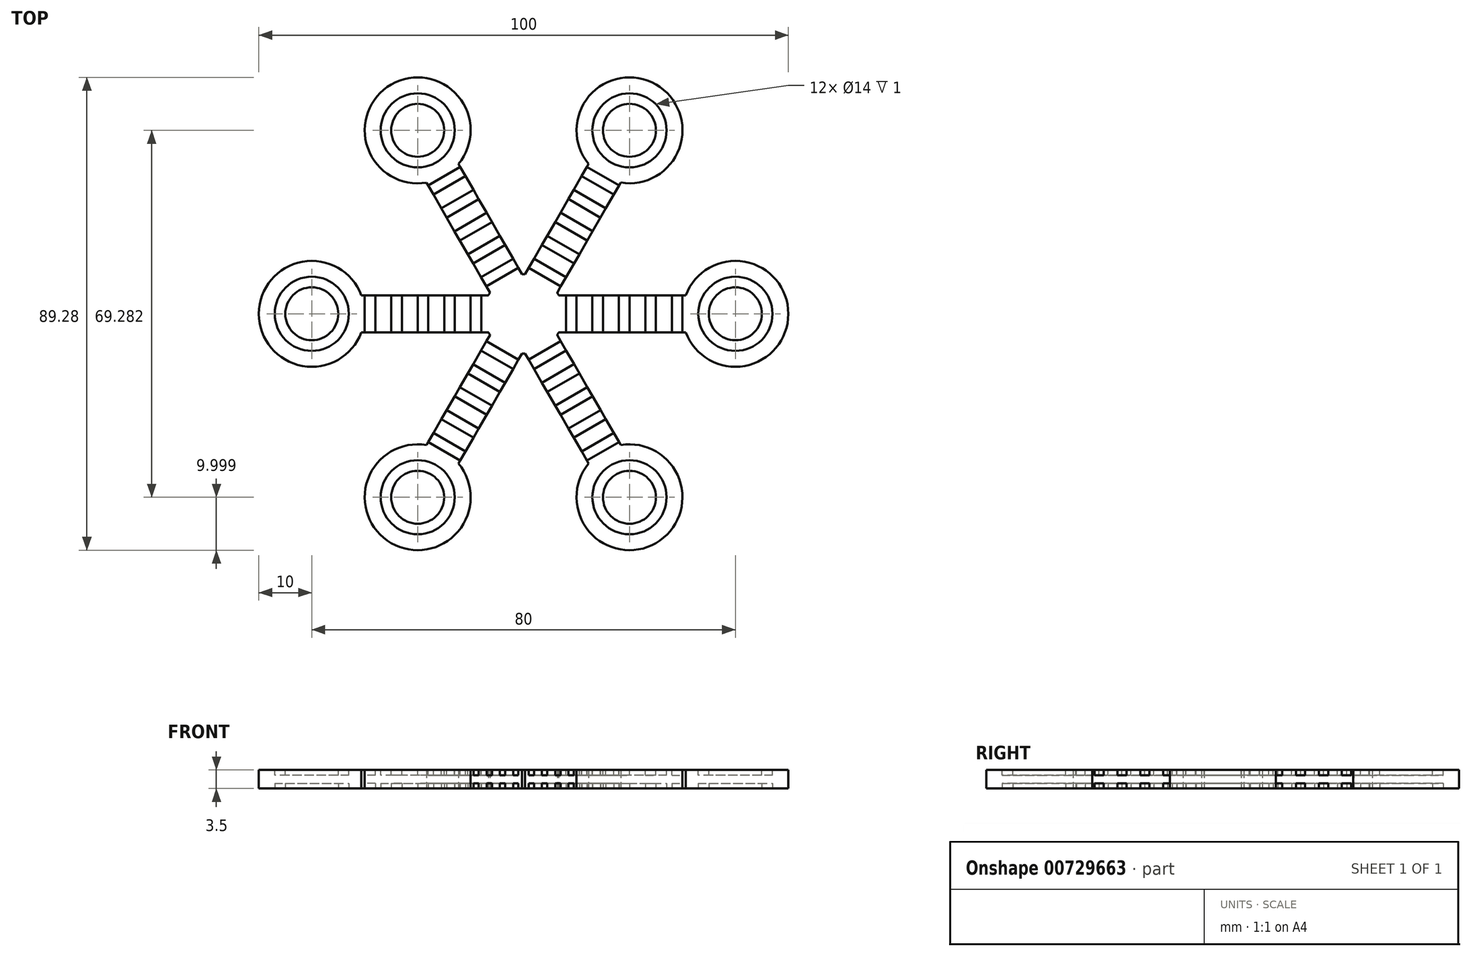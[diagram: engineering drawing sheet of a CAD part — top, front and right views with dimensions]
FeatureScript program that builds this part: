
annotation { "Feature Type Name" : "Feature", "Feature Type Description" : "" }
export const myFeature = defineFeature(function(context is Context, id is Id, definition is map)
    precondition{}
    {
        {
            var Q0;
            Q0=qCreatedBy(makeId("Top.planeOp"),FACE);
            var sketch = newSketch(context, id + "F0", { "sketchPlane" : qUnion([Q0])});
            skCircle(sketch, "E0", {"center": v(0, 0) * mm, "radius": 7.5 * mm});
            skLineSegment(sketch, "E1.bottom", {"start": v(6.63, 3.5) * mm, "end": v(40.15, 3.5) * mm});
            skLineSegment(sketch, "E1.top", {"start": v(6.64, -3.5) * mm, "end": v(39.85, -3.5) * mm});
            skLineSegment(sketch, "E1.right", {"start": v(40.15, 3.5) * mm, "end": v(39.85, -3.5) * mm});
            skCircle(sketch, "E2", {"center": v(40, 0) * mm, "radius": 10 * mm});
            skLineSegment(sketch, "E3.1.0", {"start": v(0.29, 7.5) * mm, "end": v(17.05, 36.52) * mm});
            skLineSegment(sketch, "E3.1.1", {"start": v(6.34, 4) * mm, "end": v(22.95, 32.76) * mm});
            skCircle(sketch, "E3.1.2", {"center": v(20, 34.64) * mm, "radius": 10 * mm});
            skLineSegment(sketch, "E3.1.3", {"start": v(17.05, 36.52) * mm, "end": v(22.95, 32.76) * mm});
            skLineSegment(sketch, "E3.2.0", {"start": v(-6.35, 4) * mm, "end": v(-23.1, 33.02) * mm});
            skLineSegment(sketch, "E3.2.1", {"start": v(-0.3, 7.5) * mm, "end": v(-16.9, 36.26) * mm});
            skCircle(sketch, "E3.2.2", {"center": v(-20, 34.64) * mm, "radius": 10 * mm});
            skLineSegment(sketch, "E3.2.3", {"start": v(-23.1, 33.02) * mm, "end": v(-16.9, 36.26) * mm});
            skLineSegment(sketch, "E3.3.0", {"start": v(-6.63, -3.5) * mm, "end": v(-40.15, -3.5) * mm});
            skLineSegment(sketch, "E3.3.1", {"start": v(-6.64, 3.5) * mm, "end": v(-39.85, 3.5) * mm});
            skCircle(sketch, "E3.3.2", {"center": v(-40, 0) * mm, "radius": 10 * mm});
            skLineSegment(sketch, "E3.3.3", {"start": v(-40.15, -3.5) * mm, "end": v(-39.85, 3.5) * mm});
            skLineSegment(sketch, "E3.4.0", {"start": v(-0.29, -7.5) * mm, "end": v(-17.05, -36.52) * mm});
            skLineSegment(sketch, "E3.4.1", {"start": v(-6.34, -4) * mm, "end": v(-22.95, -32.76) * mm});
            skCircle(sketch, "E3.4.2", {"center": v(-20, -34.64) * mm, "radius": 10 * mm});
            skLineSegment(sketch, "E3.4.3", {"start": v(-17.05, -36.52) * mm, "end": v(-22.95, -32.76) * mm});
            skLineSegment(sketch, "E3.5.0", {"start": v(6.35, -4) * mm, "end": v(23.1, -33.02) * mm});
            skLineSegment(sketch, "E3.5.1", {"start": v(0.3, -7.5) * mm, "end": v(16.9, -36.26) * mm});
            skCircle(sketch, "E3.5.2", {"center": v(20, -34.64) * mm, "radius": 10 * mm});
            skLineSegment(sketch, "E3.5.3", {"start": v(23.1, -33.02) * mm, "end": v(16.9, -36.26) * mm});
            skSolve(sketch);
        }
        {
            var Q0;
            {var subQ0=sQuery(id+"F0.wireOp",EDGE,"E3.3.3");Q0=makeQuery(id+"F0.imprint","IMPRINT",FACE,{"disambiguationData":[TD([[makeQuery(id+"F0.imprint","IMPRINT",EDGE,{"derivedFrom":subQ0}),1.0]])]});}
            var Q1;
            {var subQ0=sQuery(id+"F0.wireOp",EDGE,"E3.3.0");var subQ1=sQuery(id+"F0.wireOp",EDGE,"E0");var subQ2=makeQuery(id+"F0.imprint","INTERSECT",VERTEX,{"derivedFrom":[subQ1,subQ0]});Q1=makeQuery(id+"F0.imprint","IMPRINT",FACE,{"disambiguationData":[TD([[makeQuery(id+"F0.imprint","IMPRINT",EDGE,{"disambiguationData":[TD([[subQ2,1.0]])],"derivedFrom":subQ1}),-1.0]])]});}
            var Q2;
            {var subQ0=sQuery(id+"F0.wireOp",EDGE,"E3.2.3");Q2=makeQuery(id+"F0.imprint","IMPRINT",FACE,{"disambiguationData":[TD([[makeQuery(id+"F0.imprint","IMPRINT",EDGE,{"derivedFrom":subQ0}),1.0]])]});}
            var Q3;
            {var subQ0=sQuery(id+"F0.wireOp",EDGE,"E3.2.3");Q3=makeQuery(id+"F0.imprint","IMPRINT",FACE,{"disambiguationData":[TD([[makeQuery(id+"F0.imprint","IMPRINT",EDGE,{"derivedFrom":subQ0}),-1.0]])]});}
            var Q4;
            {var subQ0=sQuery(id+"F0.wireOp",EDGE,"E3.3.3");Q4=makeQuery(id+"F0.imprint","IMPRINT",FACE,{"disambiguationData":[TD([[makeQuery(id+"F0.imprint","IMPRINT",EDGE,{"derivedFrom":subQ0}),-1.0]])]});}
            var Q5;
            {var subQ0=sQuery(id+"F0.wireOp",EDGE,"E3.1.3");Q5=makeQuery(id+"F0.imprint","IMPRINT",FACE,{"disambiguationData":[TD([[makeQuery(id+"F0.imprint","IMPRINT",EDGE,{"derivedFrom":subQ0}),1.0]])]});}
            var Q6;
            {var subQ0=sQuery(id+"F0.wireOp",EDGE,"E3.1.3");Q6=makeQuery(id+"F0.imprint","IMPRINT",FACE,{"disambiguationData":[TD([[makeQuery(id+"F0.imprint","IMPRINT",EDGE,{"derivedFrom":subQ0}),-1.0]])]});}
            var Q7;
            {var subQ0=sQuery(id+"F0.wireOp",EDGE,"E3.1.0");var subQ1=sQuery(id+"F0.wireOp",EDGE,"E0");var subQ2=makeQuery(id+"F0.imprint","INTERSECT",VERTEX,{"derivedFrom":[subQ1,subQ0]});Q7=makeQuery(id+"F0.imprint","IMPRINT",FACE,{"disambiguationData":[TD([[makeQuery(id+"F0.imprint","IMPRINT",EDGE,{"disambiguationData":[TD([[subQ2,1.0]])],"derivedFrom":subQ1}),-1.0]])]});}
            var Q8;
            {var subQ0=sQuery(id+"F0.wireOp",EDGE,"E0");var subQ8=makeQuery(id+"F0.imprint","INTERSECT",VERTEX,{"derivedFrom":[subQ0,sQuery(id+"F0.wireOp",EDGE,"E1.bottom")]});Q8=makeQuery(id+"F0.imprint","IMPRINT",FACE,{"disambiguationData":[TD([[makeQuery(id+"F0.imprint","IMPRINT",EDGE,{"disambiguationData":[TD([[subQ8,-1.0]])],"derivedFrom":subQ0}),1.0]])]});}
            var Q9;
            {var subQ0=sQuery(id+"F0.wireOp",EDGE,"E1.bottom");var subQ1=sQuery(id+"F0.wireOp",EDGE,"E0");var subQ2=makeQuery(id+"F0.imprint","INTERSECT",VERTEX,{"derivedFrom":[subQ1,subQ0]});Q9=makeQuery(id+"F0.imprint","IMPRINT",FACE,{"disambiguationData":[TD([[makeQuery(id+"F0.imprint","IMPRINT",EDGE,{"disambiguationData":[TD([[subQ2,1.0]])],"derivedFrom":subQ1}),-1.0]])]});}
            var Q10;
            {var subQ0=sQuery(id+"F0.wireOp",EDGE,"E1.right");Q10=makeQuery(id+"F0.imprint","IMPRINT",FACE,{"disambiguationData":[TD([[makeQuery(id+"F0.imprint","IMPRINT",EDGE,{"derivedFrom":subQ0}),-1.0]])]});}
            var Q11;
            {var subQ0=sQuery(id+"F0.wireOp",EDGE,"E1.right");Q11=makeQuery(id+"F0.imprint","IMPRINT",FACE,{"disambiguationData":[TD([[makeQuery(id+"F0.imprint","IMPRINT",EDGE,{"derivedFrom":subQ0}),1.0]])]});}
            var Q12;
            {var subQ0=sQuery(id+"F0.wireOp",EDGE,"E3.5.3");Q12=makeQuery(id+"F0.imprint","IMPRINT",FACE,{"disambiguationData":[TD([[makeQuery(id+"F0.imprint","IMPRINT",EDGE,{"derivedFrom":subQ0}),1.0]])]});}
            var Q13;
            {var subQ0=sQuery(id+"F0.wireOp",EDGE,"E3.5.3");Q13=makeQuery(id+"F0.imprint","IMPRINT",FACE,{"disambiguationData":[TD([[makeQuery(id+"F0.imprint","IMPRINT",EDGE,{"derivedFrom":subQ0}),-1.0]])]});}
            var Q14;
            {var subQ0=sQuery(id+"F0.wireOp",EDGE,"E3.5.0");var subQ1=sQuery(id+"F0.wireOp",EDGE,"E0");var subQ2=makeQuery(id+"F0.imprint","INTERSECT",VERTEX,{"derivedFrom":[subQ1,subQ0]});Q14=makeQuery(id+"F0.imprint","IMPRINT",FACE,{"disambiguationData":[TD([[makeQuery(id+"F0.imprint","IMPRINT",EDGE,{"disambiguationData":[TD([[subQ2,1.0]])],"derivedFrom":subQ1}),-1.0]])]});}
            var Q15;
            {var subQ0=sQuery(id+"F0.wireOp",EDGE,"E3.4.0");var subQ1=sQuery(id+"F0.wireOp",EDGE,"E0");var subQ2=makeQuery(id+"F0.imprint","INTERSECT",VERTEX,{"derivedFrom":[subQ1,subQ0]});Q15=makeQuery(id+"F0.imprint","IMPRINT",FACE,{"disambiguationData":[TD([[makeQuery(id+"F0.imprint","IMPRINT",EDGE,{"disambiguationData":[TD([[subQ2,1.0]])],"derivedFrom":subQ1}),-1.0]])]});}
            var Q16;
            {var subQ0=sQuery(id+"F0.wireOp",EDGE,"E3.4.3");Q16=makeQuery(id+"F0.imprint","IMPRINT",FACE,{"disambiguationData":[TD([[makeQuery(id+"F0.imprint","IMPRINT",EDGE,{"derivedFrom":subQ0}),-1.0]])]});}
            var Q17;
            {var subQ0=sQuery(id+"F0.wireOp",EDGE,"E3.4.3");Q17=makeQuery(id+"F0.imprint","IMPRINT",FACE,{"disambiguationData":[TD([[makeQuery(id+"F0.imprint","IMPRINT",EDGE,{"derivedFrom":subQ0}),1.0]])]});}
            var Q18;
            {var subQ0=sQuery(id+"F0.wireOp",EDGE,"E3.2.0");var subQ1=sQuery(id+"F0.wireOp",EDGE,"E0");var subQ2=makeQuery(id+"F0.imprint","INTERSECT",VERTEX,{"derivedFrom":[subQ1,subQ0]});Q18=makeQuery(id+"F0.imprint","IMPRINT",FACE,{"disambiguationData":[TD([[makeQuery(id+"F0.imprint","IMPRINT",EDGE,{"disambiguationData":[TD([[subQ2,1.0]])],"derivedFrom":subQ1}),-1.0]])]});}
            extrude(context, id + "F1", {"entities" : qUnion([Q0, Q1, Q2, Q3, Q4, Q5, Q6, Q7, Q8, Q9, Q10, Q11, Q12, Q13, Q14, Q15, Q16, Q17, Q18]), "depth" : 3.5 * mm, "offsetDistance" : 25 * mm});
        }
        {
            var Q0;
            Q0=makeQuery(id+"F1.opExtrude","CAP_FACE",FACE,{"disambiguationData":[OSD([sQuery(id+"F0.wireOp",EDGE,"E0"),sQuery(id+"F0.wireOp",EDGE,"E1.bottom"),sQuery(id+"F0.wireOp",EDGE,"E1.top"),sQuery(id+"F0.wireOp",EDGE,"E2"),sQuery(id+"F0.wireOp",EDGE,"E3.1.0"),sQuery(id+"F0.wireOp",EDGE,"E3.1.1"),sQuery(id+"F0.wireOp",EDGE,"E3.1.2"),sQuery(id+"F0.wireOp",EDGE,"E3.2.0"),sQuery(id+"F0.wireOp",EDGE,"E3.2.1"),sQuery(id+"F0.wireOp",EDGE,"E3.2.2"),sQuery(id+"F0.wireOp",EDGE,"E3.3.0"),sQuery(id+"F0.wireOp",EDGE,"E3.3.1"),sQuery(id+"F0.wireOp",EDGE,"E3.3.2"),sQuery(id+"F0.wireOp",EDGE,"E3.4.0"),sQuery(id+"F0.wireOp",EDGE,"E3.4.1"),sQuery(id+"F0.wireOp",EDGE,"E3.4.2"),sQuery(id+"F0.wireOp",EDGE,"E3.5.0"),sQuery(id+"F0.wireOp",EDGE,"E3.5.1"),sQuery(id+"F0.wireOp",EDGE,"E3.5.2")])],"isStart":false});
            var sketch = newSketch(context, id + "F2", { "sketchPlane" : qUnion([Q0])});
            skLineSegment(sketch, "E4.bottom", {"start": v(8, 3.5) * mm, "end": v(10, 3.5) * mm});
            skLineSegment(sketch, "E4.top", {"start": v(8, -3.5) * mm, "end": v(10, -3.5) * mm});
            skLineSegment(sketch, "E4.left", {"start": v(8, 3.5) * mm, "end": v(8, -3.5) * mm});
            skLineSegment(sketch, "E4.right", {"start": v(10, 3.5) * mm, "end": v(10, -3.5) * mm});
            skLineSegment(sketch, "E5.1.0.0", {"start": v(13, -3.5) * mm, "end": v(15, -3.5) * mm});
            skLineSegment(sketch, "E5.1.0.1", {"start": v(13, 3.5) * mm, "end": v(15, 3.5) * mm});
            skLineSegment(sketch, "E5.1.0.2", {"start": v(13, 3.5) * mm, "end": v(13, -3.5) * mm});
            skLineSegment(sketch, "E5.1.0.3", {"start": v(15, 3.5) * mm, "end": v(15, -3.5) * mm});
            skLineSegment(sketch, "E5.2.0.0", {"start": v(18, -3.5) * mm, "end": v(20, -3.5) * mm});
            skLineSegment(sketch, "E5.2.0.1", {"start": v(18, 3.5) * mm, "end": v(20, 3.5) * mm});
            skLineSegment(sketch, "E5.2.0.2", {"start": v(18, 3.5) * mm, "end": v(18, -3.5) * mm});
            skLineSegment(sketch, "E5.2.0.3", {"start": v(20, 3.5) * mm, "end": v(20, -3.5) * mm});
            skLineSegment(sketch, "E5.3.0.0", {"start": v(23, -3.5) * mm, "end": v(25, -3.5) * mm});
            skLineSegment(sketch, "E5.3.0.1", {"start": v(23, 3.5) * mm, "end": v(25, 3.5) * mm});
            skLineSegment(sketch, "E5.3.0.2", {"start": v(23, 3.5) * mm, "end": v(23, -3.5) * mm});
            skLineSegment(sketch, "E5.3.0.3", {"start": v(25, 3.5) * mm, "end": v(25, -3.5) * mm});
            skLineSegment(sketch, "E5.4.0.0", {"start": v(28, -3.5) * mm, "end": v(30, -3.5) * mm});
            skLineSegment(sketch, "E5.4.0.1", {"start": v(28, 3.5) * mm, "end": v(30, 3.5) * mm});
            skLineSegment(sketch, "E5.4.0.2", {"start": v(28, 3.5) * mm, "end": v(28, -3.5) * mm});
            skLineSegment(sketch, "E5.4.0.3", {"start": v(30, 3.5) * mm, "end": v(30, -3.5) * mm});
            skLineSegment(sketch, "E5.direction1", {"start": v(8, -3.5) * mm, "end": v(13, -3.5) * mm, "construction": true});
            skLineSegment(sketch, "E6.1.0", {"start": v(3.47, 13) * mm, "end": v(9.53, 9.51) * mm});
            skLineSegment(sketch, "E6.1.1", {"start": v(0.97, 8.68) * mm, "end": v(1.97, 10.41) * mm});
            skLineSegment(sketch, "E6.1.2", {"start": v(4.47, 14.74) * mm, "end": v(10.53, 11.24) * mm});
            skLineSegment(sketch, "E6.1.3", {"start": v(12.03, 13.84) * mm, "end": v(13.03, 15.57) * mm});
            skLineSegment(sketch, "E6.1.4", {"start": v(0.97, 8.68) * mm, "end": v(7.03, 5.18) * mm});
            skLineSegment(sketch, "E6.1.5", {"start": v(5.97, 17.34) * mm, "end": v(6.97, 19.07) * mm});
            skLineSegment(sketch, "E6.1.6", {"start": v(7.03, 5.18) * mm, "end": v(9.53, 9.51) * mm, "construction": true});
            skLineSegment(sketch, "E6.1.7", {"start": v(1.97, 10.41) * mm, "end": v(8.03, 6.91) * mm});
            skLineSegment(sketch, "E6.1.8", {"start": v(9.47, 23.4) * mm, "end": v(15.53, 19.9) * mm});
            skLineSegment(sketch, "E6.1.9", {"start": v(5.97, 17.34) * mm, "end": v(12.03, 13.84) * mm});
            skLineSegment(sketch, "E6.1.10", {"start": v(11.97, 27.73) * mm, "end": v(18.03, 24.23) * mm});
            skLineSegment(sketch, "E6.1.11", {"start": v(9.53, 9.51) * mm, "end": v(10.53, 11.24) * mm});
            skLineSegment(sketch, "E6.1.12", {"start": v(8.47, 21.67) * mm, "end": v(9.47, 23.4) * mm});
            skLineSegment(sketch, "E6.1.13", {"start": v(6.97, 19.07) * mm, "end": v(13.03, 15.57) * mm});
            skLineSegment(sketch, "E6.1.14", {"start": v(10.97, 26) * mm, "end": v(17.03, 22.5) * mm});
            skLineSegment(sketch, "E6.1.15", {"start": v(3.47, 13) * mm, "end": v(4.47, 14.74) * mm});
            skLineSegment(sketch, "E6.1.16", {"start": v(8.47, 21.67) * mm, "end": v(14.53, 18.17) * mm});
            skLineSegment(sketch, "E6.1.17", {"start": v(14.53, 18.17) * mm, "end": v(15.53, 19.9) * mm});
            skLineSegment(sketch, "E6.1.18", {"start": v(10.97, 26) * mm, "end": v(11.97, 27.73) * mm});
            skLineSegment(sketch, "E6.1.19", {"start": v(17.03, 22.5) * mm, "end": v(18.03, 24.23) * mm});
            skLineSegment(sketch, "E6.1.20", {"start": v(7.03, 5.18) * mm, "end": v(8.03, 6.91) * mm});
            skLineSegment(sketch, "E6.2.0", {"start": v(-9.53, 9.5) * mm, "end": v(-3.47, 13) * mm});
            skLineSegment(sketch, "E6.2.1", {"start": v(-7.03, 5.18) * mm, "end": v(-8.03, 6.91) * mm});
            skLineSegment(sketch, "E6.2.2", {"start": v(-10.53, 11.24) * mm, "end": v(-4.47, 14.74) * mm});
            skLineSegment(sketch, "E6.2.3", {"start": v(-5.97, 17.34) * mm, "end": v(-6.97, 19.07) * mm});
            skLineSegment(sketch, "E6.2.4", {"start": v(-7.03, 5.18) * mm, "end": v(-0.97, 8.67) * mm});
            skLineSegment(sketch, "E6.2.5", {"start": v(-12.03, 13.84) * mm, "end": v(-13.03, 15.57) * mm});
            skLineSegment(sketch, "E6.2.6", {"start": v(-0.97, 8.67) * mm, "end": v(-3.47, 13) * mm, "construction": true});
            skLineSegment(sketch, "E6.2.7", {"start": v(-8.03, 6.91) * mm, "end": v(-1.97, 10.4) * mm});
            skLineSegment(sketch, "E6.2.8", {"start": v(-15.53, 19.9) * mm, "end": v(-9.47, 23.4) * mm});
            skLineSegment(sketch, "E6.2.9", {"start": v(-12.03, 13.84) * mm, "end": v(-5.97, 17.34) * mm});
            skLineSegment(sketch, "E6.2.10", {"start": v(-18.03, 24.23) * mm, "end": v(-11.97, 27.73) * mm});
            skLineSegment(sketch, "E6.2.11", {"start": v(-3.47, 13) * mm, "end": v(-4.47, 14.74) * mm});
            skLineSegment(sketch, "E6.2.12", {"start": v(-14.53, 18.17) * mm, "end": v(-15.53, 19.9) * mm});
            skLineSegment(sketch, "E6.2.13", {"start": v(-13.03, 15.57) * mm, "end": v(-6.97, 19.07) * mm});
            skLineSegment(sketch, "E6.2.14", {"start": v(-17.03, 22.5) * mm, "end": v(-10.97, 26) * mm});
            skLineSegment(sketch, "E6.2.15", {"start": v(-9.53, 9.5) * mm, "end": v(-10.53, 11.24) * mm});
            skLineSegment(sketch, "E6.2.16", {"start": v(-14.53, 18.17) * mm, "end": v(-8.47, 21.67) * mm});
            skLineSegment(sketch, "E6.2.17", {"start": v(-8.47, 21.67) * mm, "end": v(-9.47, 23.4) * mm});
            skLineSegment(sketch, "E6.2.18", {"start": v(-17.03, 22.5) * mm, "end": v(-18.03, 24.23) * mm});
            skLineSegment(sketch, "E6.2.19", {"start": v(-10.97, 26) * mm, "end": v(-11.97, 27.73) * mm});
            skLineSegment(sketch, "E6.2.20", {"start": v(-0.97, 8.67) * mm, "end": v(-1.97, 10.4) * mm});
            skLineSegment(sketch, "E6.3.0", {"start": v(-13, -3.5) * mm, "end": v(-13, 3.5) * mm});
            skLineSegment(sketch, "E6.3.1", {"start": v(-8, -3.5) * mm, "end": v(-10, -3.5) * mm});
            skLineSegment(sketch, "E6.3.2", {"start": v(-15, -3.5) * mm, "end": v(-15, 3.5) * mm});
            skLineSegment(sketch, "E6.3.3", {"start": v(-18, 3.5) * mm, "end": v(-20, 3.5) * mm});
            skLineSegment(sketch, "E6.3.4", {"start": v(-8, -3.5) * mm, "end": v(-8, 3.5) * mm});
            skLineSegment(sketch, "E6.3.5", {"start": v(-18, -3.5) * mm, "end": v(-20, -3.5) * mm});
            skLineSegment(sketch, "E6.3.6", {"start": v(-8, 3.5) * mm, "end": v(-13, 3.5) * mm, "construction": true});
            skLineSegment(sketch, "E6.3.7", {"start": v(-10, -3.5) * mm, "end": v(-10, 3.5) * mm});
            skLineSegment(sketch, "E6.3.8", {"start": v(-25, -3.5) * mm, "end": v(-25, 3.5) * mm});
            skLineSegment(sketch, "E6.3.9", {"start": v(-18, -3.5) * mm, "end": v(-18, 3.5) * mm});
            skLineSegment(sketch, "E6.3.10", {"start": v(-30, -3.5) * mm, "end": v(-30, 3.5) * mm});
            skLineSegment(sketch, "E6.3.11", {"start": v(-13, 3.5) * mm, "end": v(-15, 3.5) * mm});
            skLineSegment(sketch, "E6.3.12", {"start": v(-23, -3.5) * mm, "end": v(-25, -3.5) * mm});
            skLineSegment(sketch, "E6.3.13", {"start": v(-20, -3.5) * mm, "end": v(-20, 3.5) * mm});
            skLineSegment(sketch, "E6.3.14", {"start": v(-28, -3.5) * mm, "end": v(-28, 3.5) * mm});
            skLineSegment(sketch, "E6.3.15", {"start": v(-13, -3.5) * mm, "end": v(-15, -3.5) * mm});
            skLineSegment(sketch, "E6.3.16", {"start": v(-23, -3.5) * mm, "end": v(-23, 3.5) * mm});
            skLineSegment(sketch, "E6.3.17", {"start": v(-23, 3.5) * mm, "end": v(-25, 3.5) * mm});
            skLineSegment(sketch, "E6.3.18", {"start": v(-28, -3.5) * mm, "end": v(-30, -3.5) * mm});
            skLineSegment(sketch, "E6.3.19", {"start": v(-28, 3.5) * mm, "end": v(-30, 3.5) * mm});
            skLineSegment(sketch, "E6.3.20", {"start": v(-8, 3.5) * mm, "end": v(-10, 3.5) * mm});
            skLineSegment(sketch, "E6.4.0", {"start": v(-3.47, -13) * mm, "end": v(-9.53, -9.51) * mm});
            skLineSegment(sketch, "E6.4.1", {"start": v(-0.97, -8.68) * mm, "end": v(-1.97, -10.41) * mm});
            skLineSegment(sketch, "E6.4.2", {"start": v(-4.47, -14.74) * mm, "end": v(-10.53, -11.24) * mm});
            skLineSegment(sketch, "E6.4.3", {"start": v(-12.03, -13.84) * mm, "end": v(-13.03, -15.57) * mm});
            skLineSegment(sketch, "E6.4.4", {"start": v(-0.97, -8.68) * mm, "end": v(-7.03, -5.18) * mm});
            skLineSegment(sketch, "E6.4.5", {"start": v(-5.97, -17.34) * mm, "end": v(-6.97, -19.07) * mm});
            skLineSegment(sketch, "E6.4.6", {"start": v(-7.03, -5.18) * mm, "end": v(-9.53, -9.51) * mm, "construction": true});
            skLineSegment(sketch, "E6.4.7", {"start": v(-1.97, -10.41) * mm, "end": v(-8.03, -6.91) * mm});
            skLineSegment(sketch, "E6.4.8", {"start": v(-9.47, -23.4) * mm, "end": v(-15.53, -19.9) * mm});
            skLineSegment(sketch, "E6.4.9", {"start": v(-5.97, -17.34) * mm, "end": v(-12.03, -13.84) * mm});
            skLineSegment(sketch, "E6.4.10", {"start": v(-11.97, -27.73) * mm, "end": v(-18.03, -24.23) * mm});
            skLineSegment(sketch, "E6.4.11", {"start": v(-9.53, -9.51) * mm, "end": v(-10.53, -11.24) * mm});
            skLineSegment(sketch, "E6.4.12", {"start": v(-8.47, -21.67) * mm, "end": v(-9.47, -23.4) * mm});
            skLineSegment(sketch, "E6.4.13", {"start": v(-6.97, -19.07) * mm, "end": v(-13.03, -15.57) * mm});
            skLineSegment(sketch, "E6.4.14", {"start": v(-10.97, -26) * mm, "end": v(-17.03, -22.5) * mm});
            skLineSegment(sketch, "E6.4.15", {"start": v(-3.47, -13) * mm, "end": v(-4.47, -14.74) * mm});
            skLineSegment(sketch, "E6.4.16", {"start": v(-8.47, -21.67) * mm, "end": v(-14.53, -18.17) * mm});
            skLineSegment(sketch, "E6.4.17", {"start": v(-14.53, -18.17) * mm, "end": v(-15.53, -19.9) * mm});
            skLineSegment(sketch, "E6.4.18", {"start": v(-10.97, -26) * mm, "end": v(-11.97, -27.73) * mm});
            skLineSegment(sketch, "E6.4.19", {"start": v(-17.03, -22.5) * mm, "end": v(-18.03, -24.23) * mm});
            skLineSegment(sketch, "E6.4.20", {"start": v(-7.03, -5.18) * mm, "end": v(-8.03, -6.91) * mm});
            skLineSegment(sketch, "E6.5.0", {"start": v(9.53, -9.5) * mm, "end": v(3.47, -13) * mm});
            skLineSegment(sketch, "E6.5.1", {"start": v(7.03, -5.18) * mm, "end": v(8.03, -6.91) * mm});
            skLineSegment(sketch, "E6.5.2", {"start": v(10.53, -11.24) * mm, "end": v(4.47, -14.74) * mm});
            skLineSegment(sketch, "E6.5.3", {"start": v(5.97, -17.34) * mm, "end": v(6.97, -19.07) * mm});
            skLineSegment(sketch, "E6.5.4", {"start": v(7.03, -5.18) * mm, "end": v(0.97, -8.67) * mm});
            skLineSegment(sketch, "E6.5.5", {"start": v(12.03, -13.84) * mm, "end": v(13.03, -15.57) * mm});
            skLineSegment(sketch, "E6.5.6", {"start": v(0.97, -8.67) * mm, "end": v(3.47, -13) * mm, "construction": true});
            skLineSegment(sketch, "E6.5.7", {"start": v(8.03, -6.91) * mm, "end": v(1.97, -10.4) * mm});
            skLineSegment(sketch, "E6.5.8", {"start": v(15.53, -19.9) * mm, "end": v(9.47, -23.4) * mm});
            skLineSegment(sketch, "E6.5.9", {"start": v(12.03, -13.84) * mm, "end": v(5.97, -17.34) * mm});
            skLineSegment(sketch, "E6.5.10", {"start": v(18.03, -24.23) * mm, "end": v(11.97, -27.73) * mm});
            skLineSegment(sketch, "E6.5.11", {"start": v(3.47, -13) * mm, "end": v(4.47, -14.74) * mm});
            skLineSegment(sketch, "E6.5.12", {"start": v(14.53, -18.17) * mm, "end": v(15.53, -19.9) * mm});
            skLineSegment(sketch, "E6.5.13", {"start": v(13.03, -15.57) * mm, "end": v(6.97, -19.07) * mm});
            skLineSegment(sketch, "E6.5.14", {"start": v(17.03, -22.5) * mm, "end": v(10.97, -26) * mm});
            skLineSegment(sketch, "E6.5.15", {"start": v(9.53, -9.5) * mm, "end": v(10.53, -11.24) * mm});
            skLineSegment(sketch, "E6.5.16", {"start": v(14.53, -18.17) * mm, "end": v(8.47, -21.67) * mm});
            skLineSegment(sketch, "E6.5.17", {"start": v(8.47, -21.67) * mm, "end": v(9.47, -23.4) * mm});
            skLineSegment(sketch, "E6.5.18", {"start": v(17.03, -22.5) * mm, "end": v(18.03, -24.23) * mm});
            skLineSegment(sketch, "E6.5.19", {"start": v(10.97, -26) * mm, "end": v(11.97, -27.73) * mm});
            skLineSegment(sketch, "E6.5.20", {"start": v(0.97, -8.67) * mm, "end": v(1.97, -10.4) * mm});
            skPoint(sketch, "E6.center", {"position": v(0, 0) * mm});
            skCircle(sketch, "E7", {"center": v(40, 0) * mm, "radius": 7 * mm});
            skCircle(sketch, "E8", {"center": v(40, 0) * mm, "radius": 5 * mm});
            skCircle(sketch, "E9.1.0", {"center": v(20, 34.64) * mm, "radius": 7 * mm});
            skCircle(sketch, "E9.1.1", {"center": v(20, 34.64) * mm, "radius": 5 * mm});
            skCircle(sketch, "E9.2.0", {"center": v(-20, 34.64) * mm, "radius": 7 * mm});
            skCircle(sketch, "E9.2.1", {"center": v(-20, 34.64) * mm, "radius": 5 * mm});
            skCircle(sketch, "E9.3.0", {"center": v(-40, 0) * mm, "radius": 7 * mm});
            skCircle(sketch, "E9.3.1", {"center": v(-40, 0) * mm, "radius": 5 * mm});
            skCircle(sketch, "E9.4.0", {"center": v(-20, -34.64) * mm, "radius": 7 * mm});
            skCircle(sketch, "E9.4.1", {"center": v(-20, -34.64) * mm, "radius": 5 * mm});
            skCircle(sketch, "E9.5.0", {"center": v(20, -34.64) * mm, "radius": 7 * mm});
            skCircle(sketch, "E9.5.1", {"center": v(20, -34.64) * mm, "radius": 5 * mm});
            skSolve(sketch);
        }
        {
            var Q0;
            Q0=makeQuery(id+"F2.imprint","IMPRINT",FACE,{"disambiguationData":[TD([[makeQuery(id+"F2.imprint","IMPRINT",EDGE,{"derivedFrom":sQuery(id+"F2.wireOp",EDGE,"E6.4.10")}),-1.0]])]});
            var Q1;
            Q1=makeQuery(id+"F2.imprint","IMPRINT",FACE,{"disambiguationData":[TD([[makeQuery(id+"F2.imprint","IMPRINT",EDGE,{"derivedFrom":sQuery(id+"F2.wireOp",EDGE,"E6.4.8")}),-1.0]])]});
            var Q2;
            Q2=makeQuery(id+"F2.imprint","IMPRINT",FACE,{"disambiguationData":[TD([[makeQuery(id+"F2.imprint","IMPRINT",EDGE,{"derivedFrom":sQuery(id+"F2.wireOp",EDGE,"E6.4.3")}),1.0]])]});
            var Q3;
            Q3=makeQuery(id+"F2.imprint","IMPRINT",FACE,{"disambiguationData":[TD([[makeQuery(id+"F2.imprint","IMPRINT",EDGE,{"derivedFrom":sQuery(id+"F2.wireOp",EDGE,"E6.4.0")}),1.0]])]});
            var Q4;
            Q4=makeQuery(id+"F2.imprint","IMPRINT",FACE,{"disambiguationData":[TD([[makeQuery(id+"F2.imprint","IMPRINT",EDGE,{"derivedFrom":sQuery(id+"F2.wireOp",EDGE,"E6.4.1")}),-1.0]])]});
            var Q5;
            Q5=makeQuery(id+"F2.imprint","IMPRINT",FACE,{"disambiguationData":[TD([[makeQuery(id+"F2.imprint","IMPRINT",EDGE,{"derivedFrom":sQuery(id+"F2.wireOp",EDGE,"E6.5.1")}),-1.0]])]});
            var Q6;
            Q6=makeQuery(id+"F2.imprint","IMPRINT",FACE,{"disambiguationData":[TD([[makeQuery(id+"F2.imprint","IMPRINT",EDGE,{"derivedFrom":sQuery(id+"F2.wireOp",EDGE,"E6.5.0")}),1.0]])]});
            var Q7;
            Q7=makeQuery(id+"F2.imprint","IMPRINT",FACE,{"disambiguationData":[TD([[makeQuery(id+"F2.imprint","IMPRINT",EDGE,{"derivedFrom":sQuery(id+"F2.wireOp",EDGE,"E6.5.3")}),1.0]])]});
            var Q8;
            Q8=makeQuery(id+"F2.imprint","IMPRINT",FACE,{"disambiguationData":[TD([[makeQuery(id+"F2.imprint","IMPRINT",EDGE,{"derivedFrom":sQuery(id+"F2.wireOp",EDGE,"E6.5.8")}),-1.0]])]});
            var Q9;
            Q9=makeQuery(id+"F2.imprint","IMPRINT",FACE,{"disambiguationData":[TD([[makeQuery(id+"F2.imprint","IMPRINT",EDGE,{"derivedFrom":sQuery(id+"F2.wireOp",EDGE,"E6.5.10")}),-1.0]])]});
            var Q10;
            Q10=makeQuery(id+"F2.imprint","IMPRINT",FACE,{"disambiguationData":[TD([[makeQuery(id+"F2.imprint","IMPRINT",EDGE,{"derivedFrom":sQuery(id+"F2.wireOp",EDGE,"E5.4.0.0")}),1.0]])]});
            var Q11;
            Q11=makeQuery(id+"F2.imprint","IMPRINT",FACE,{"disambiguationData":[TD([[makeQuery(id+"F2.imprint","IMPRINT",EDGE,{"derivedFrom":sQuery(id+"F2.wireOp",EDGE,"E5.2.0.0")}),1.0]])]});
            var Q12;
            Q12=makeQuery(id+"F2.imprint","IMPRINT",FACE,{"disambiguationData":[TD([[makeQuery(id+"F2.imprint","IMPRINT",EDGE,{"derivedFrom":sQuery(id+"F2.wireOp",EDGE,"E5.1.0.0")}),1.0]])]});
            var Q13;
            Q13=makeQuery(id+"F2.imprint","IMPRINT",FACE,{"disambiguationData":[TD([[makeQuery(id+"F2.imprint","IMPRINT",EDGE,{"derivedFrom":sQuery(id+"F2.wireOp",EDGE,"E4.bottom")}),-1.0]])]});
            var Q14;
            Q14=makeQuery(id+"F2.imprint","IMPRINT",FACE,{"disambiguationData":[TD([[makeQuery(id+"F2.imprint","IMPRINT",EDGE,{"derivedFrom":sQuery(id+"F2.wireOp",EDGE,"E6.1.10")}),-1.0]])]});
            var Q15;
            Q15=makeQuery(id+"F2.imprint","IMPRINT",FACE,{"disambiguationData":[TD([[makeQuery(id+"F2.imprint","IMPRINT",EDGE,{"derivedFrom":sQuery(id+"F2.wireOp",EDGE,"E6.1.8")}),-1.0]])]});
            var Q16;
            Q16=makeQuery(id+"F2.imprint","IMPRINT",FACE,{"disambiguationData":[TD([[makeQuery(id+"F2.imprint","IMPRINT",EDGE,{"derivedFrom":sQuery(id+"F2.wireOp",EDGE,"E6.1.3")}),1.0]])]});
            var Q17;
            Q17=makeQuery(id+"F2.imprint","IMPRINT",FACE,{"disambiguationData":[TD([[makeQuery(id+"F2.imprint","IMPRINT",EDGE,{"derivedFrom":sQuery(id+"F2.wireOp",EDGE,"E6.1.0")}),1.0]])]});
            var Q18;
            Q18=makeQuery(id+"F2.imprint","IMPRINT",FACE,{"disambiguationData":[TD([[makeQuery(id+"F2.imprint","IMPRINT",EDGE,{"derivedFrom":sQuery(id+"F2.wireOp",EDGE,"E6.1.1")}),-1.0]])]});
            var Q19;
            Q19=makeQuery(id+"F2.imprint","IMPRINT",FACE,{"disambiguationData":[TD([[makeQuery(id+"F2.imprint","IMPRINT",EDGE,{"derivedFrom":sQuery(id+"F2.wireOp",EDGE,"E6.2.1")}),-1.0]])]});
            var Q20;
            Q20=makeQuery(id+"F2.imprint","IMPRINT",FACE,{"disambiguationData":[TD([[makeQuery(id+"F2.imprint","IMPRINT",EDGE,{"derivedFrom":sQuery(id+"F2.wireOp",EDGE,"E6.2.0")}),1.0]])]});
            var Q21;
            Q21=makeQuery(id+"F2.imprint","IMPRINT",FACE,{"disambiguationData":[TD([[makeQuery(id+"F2.imprint","IMPRINT",EDGE,{"derivedFrom":sQuery(id+"F2.wireOp",EDGE,"E6.2.3")}),1.0]])]});
            var Q22;
            Q22=makeQuery(id+"F2.imprint","IMPRINT",FACE,{"disambiguationData":[TD([[makeQuery(id+"F2.imprint","IMPRINT",EDGE,{"derivedFrom":sQuery(id+"F2.wireOp",EDGE,"E6.2.8")}),-1.0]])]});
            var Q23;
            Q23=makeQuery(id+"F2.imprint","IMPRINT",FACE,{"disambiguationData":[TD([[makeQuery(id+"F2.imprint","IMPRINT",EDGE,{"derivedFrom":sQuery(id+"F2.wireOp",EDGE,"E6.2.10")}),-1.0]])]});
            var Q24;
            Q24=makeQuery(id+"F2.imprint","IMPRINT",FACE,{"disambiguationData":[TD([[makeQuery(id+"F2.imprint","IMPRINT",EDGE,{"derivedFrom":sQuery(id+"F2.wireOp",EDGE,"E6.3.1")}),-1.0]])]});
            var Q25;
            Q25=makeQuery(id+"F2.imprint","IMPRINT",FACE,{"disambiguationData":[TD([[makeQuery(id+"F2.imprint","IMPRINT",EDGE,{"derivedFrom":sQuery(id+"F2.wireOp",EDGE,"E6.3.0")}),1.0]])]});
            var Q26;
            Q26=makeQuery(id+"F2.imprint","IMPRINT",FACE,{"disambiguationData":[TD([[makeQuery(id+"F2.imprint","IMPRINT",EDGE,{"derivedFrom":sQuery(id+"F2.wireOp",EDGE,"E6.3.3")}),1.0]])]});
            var Q27;
            Q27=makeQuery(id+"F2.imprint","IMPRINT",FACE,{"disambiguationData":[TD([[makeQuery(id+"F2.imprint","IMPRINT",EDGE,{"derivedFrom":sQuery(id+"F2.wireOp",EDGE,"E6.3.8")}),-1.0]])]});
            var Q28;
            Q28=makeQuery(id+"F2.imprint","IMPRINT",FACE,{"disambiguationData":[TD([[makeQuery(id+"F2.imprint","IMPRINT",EDGE,{"derivedFrom":sQuery(id+"F2.wireOp",EDGE,"E6.3.10")}),-1.0]])]});
            var Q29;
            Q29=makeQuery(id+"F2.imprint","IMPRINT",FACE,{"disambiguationData":[TD([[makeQuery(id+"F2.imprint","IMPRINT",EDGE,{"derivedFrom":sQuery(id+"F2.wireOp",EDGE,"E9.2.0")}),1.0]])]});
            var Q30;
            Q30=makeQuery(id+"F2.imprint","IMPRINT",FACE,{"disambiguationData":[TD([[makeQuery(id+"F2.imprint","IMPRINT",EDGE,{"derivedFrom":sQuery(id+"F2.wireOp",EDGE,"E9.1.0")}),1.0]])]});
            var Q31;
            Q31=makeQuery(id+"F2.imprint","IMPRINT",FACE,{"disambiguationData":[TD([[makeQuery(id+"F2.imprint","IMPRINT",EDGE,{"derivedFrom":sQuery(id+"F2.wireOp",EDGE,"E7")}),1.0]])]});
            var Q32;
            Q32=makeQuery(id+"F2.imprint","IMPRINT",FACE,{"disambiguationData":[TD([[makeQuery(id+"F2.imprint","IMPRINT",EDGE,{"derivedFrom":sQuery(id+"F2.wireOp",EDGE,"E9.5.0")}),1.0]])]});
            var Q33;
            Q33=makeQuery(id+"F2.imprint","IMPRINT",FACE,{"disambiguationData":[TD([[makeQuery(id+"F2.imprint","IMPRINT",EDGE,{"derivedFrom":sQuery(id+"F2.wireOp",EDGE,"E9.4.0")}),1.0]])]});
            var Q34;
            Q34=makeQuery(id+"F2.imprint","IMPRINT",FACE,{"disambiguationData":[TD([[makeQuery(id+"F2.imprint","IMPRINT",EDGE,{"derivedFrom":sQuery(id+"F2.wireOp",EDGE,"E9.3.0")}),1.0]])]});
            var Q35;
            Q35=makeQuery(id+"F2.imprint","IMPRINT",FACE,{"disambiguationData":[TD([[makeQuery(id+"F2.imprint","IMPRINT",EDGE,{"derivedFrom":sQuery(id+"F2.wireOp",EDGE,"E5.3.0.0")}),1.0]])]});
            extrude(context, id + "F3", {"entities" : qUnion([Q0, Q1, Q2, Q3, Q4, Q5, Q6, Q7, Q8, Q9, Q10, Q11, Q12, Q13, Q14, Q15, Q16, Q17, Q18, Q19, Q20, Q21, Q22, Q23, Q24, Q25, Q26, Q27, Q28, Q29, Q30, Q31, Q32, Q33, Q34, Q35]), "operationType" : NewBodyOperationType.REMOVE, "oppositeDirection" : true, "depth" : 1 * mm, "offsetDistance" : 25 * mm});
        }
        {
            var Q0;
            Q0=makeQuery(id+"F1.opExtrude","CAP_FACE",FACE,{"disambiguationData":[OSD([sQuery(id+"F0.wireOp",EDGE,"E0"),sQuery(id+"F0.wireOp",EDGE,"E1.bottom"),sQuery(id+"F0.wireOp",EDGE,"E1.top"),sQuery(id+"F0.wireOp",EDGE,"E2"),sQuery(id+"F0.wireOp",EDGE,"E3.1.0"),sQuery(id+"F0.wireOp",EDGE,"E3.1.1"),sQuery(id+"F0.wireOp",EDGE,"E3.1.2"),sQuery(id+"F0.wireOp",EDGE,"E3.2.0"),sQuery(id+"F0.wireOp",EDGE,"E3.2.1"),sQuery(id+"F0.wireOp",EDGE,"E3.2.2"),sQuery(id+"F0.wireOp",EDGE,"E3.3.0"),sQuery(id+"F0.wireOp",EDGE,"E3.3.1"),sQuery(id+"F0.wireOp",EDGE,"E3.3.2"),sQuery(id+"F0.wireOp",EDGE,"E3.4.0"),sQuery(id+"F0.wireOp",EDGE,"E3.4.1"),sQuery(id+"F0.wireOp",EDGE,"E3.4.2"),sQuery(id+"F0.wireOp",EDGE,"E3.5.0"),sQuery(id+"F0.wireOp",EDGE,"E3.5.1"),sQuery(id+"F0.wireOp",EDGE,"E3.5.2")])],"isStart":true});
            var sketch = newSketch(context, id + "F4", { "sketchPlane" : qUnion([Q0])});
            skLineSegment(sketch, "E10.bottom", {"start": v(8, 3.5) * mm, "end": v(10, 3.5) * mm});
            skLineSegment(sketch, "E10.top", {"start": v(8, -3.5) * mm, "end": v(10, -3.5) * mm});
            skLineSegment(sketch, "E10.left", {"start": v(8, 3.5) * mm, "end": v(8, -3.5) * mm});
            skLineSegment(sketch, "E10.right", {"start": v(10, 3.5) * mm, "end": v(10, -3.5) * mm});
            skLineSegment(sketch, "E11.1.0.0", {"start": v(15, 3.5) * mm, "end": v(15, -3.5) * mm});
            skLineSegment(sketch, "E11.1.0.1", {"start": v(13, 3.5) * mm, "end": v(15, 3.5) * mm});
            skLineSegment(sketch, "E11.1.0.2", {"start": v(13, 3.5) * mm, "end": v(13, -3.5) * mm});
            skLineSegment(sketch, "E11.1.0.3", {"start": v(13, -3.5) * mm, "end": v(15, -3.5) * mm});
            skLineSegment(sketch, "E11.2.0.0", {"start": v(20, 3.5) * mm, "end": v(20, -3.5) * mm});
            skLineSegment(sketch, "E11.2.0.1", {"start": v(18, 3.5) * mm, "end": v(20, 3.5) * mm});
            skLineSegment(sketch, "E11.2.0.2", {"start": v(18, 3.5) * mm, "end": v(18, -3.5) * mm});
            skLineSegment(sketch, "E11.2.0.3", {"start": v(18, -3.5) * mm, "end": v(20, -3.5) * mm});
            skLineSegment(sketch, "E11.3.0.0", {"start": v(25, 3.5) * mm, "end": v(25, -3.5) * mm});
            skLineSegment(sketch, "E11.3.0.1", {"start": v(23, 3.5) * mm, "end": v(25, 3.5) * mm});
            skLineSegment(sketch, "E11.3.0.2", {"start": v(23, 3.5) * mm, "end": v(23, -3.5) * mm});
            skLineSegment(sketch, "E11.3.0.3", {"start": v(23, -3.5) * mm, "end": v(25, -3.5) * mm});
            skLineSegment(sketch, "E11.4.0.0", {"start": v(30, 3.5) * mm, "end": v(30, -3.5) * mm});
            skLineSegment(sketch, "E11.4.0.1", {"start": v(28, 3.5) * mm, "end": v(30, 3.5) * mm});
            skLineSegment(sketch, "E11.4.0.2", {"start": v(28, 3.5) * mm, "end": v(28, -3.5) * mm});
            skLineSegment(sketch, "E11.4.0.3", {"start": v(28, -3.5) * mm, "end": v(30, -3.5) * mm});
            skLineSegment(sketch, "E11.direction1", {"start": v(10, -3.5) * mm, "end": v(15, -3.5) * mm, "construction": true});
            skCircle(sketch, "E12", {"center": v(40, 0) * mm, "radius": 5 * mm});
            skCircle(sketch, "E13", {"center": v(40, 0) * mm, "radius": 7 * mm});
            skCircle(sketch, "E14.1.0", {"center": v(20, 34.64) * mm, "radius": 5 * mm});
            skCircle(sketch, "E14.1.1", {"center": v(20, 34.64) * mm, "radius": 7 * mm});
            skCircle(sketch, "E14.2.0", {"center": v(-20, 34.64) * mm, "radius": 5 * mm});
            skCircle(sketch, "E14.2.1", {"center": v(-20, 34.64) * mm, "radius": 7 * mm});
            skCircle(sketch, "E14.3.0", {"center": v(-40, 0) * mm, "radius": 5 * mm});
            skCircle(sketch, "E14.3.1", {"center": v(-40, 0) * mm, "radius": 7 * mm});
            skCircle(sketch, "E14.4.0", {"center": v(-20, -34.64) * mm, "radius": 5 * mm});
            skCircle(sketch, "E14.4.1", {"center": v(-20, -34.64) * mm, "radius": 7 * mm});
            skCircle(sketch, "E14.5.0", {"center": v(20, -34.64) * mm, "radius": 5 * mm});
            skCircle(sketch, "E14.5.1", {"center": v(20, -34.64) * mm, "radius": 7 * mm});
            skPoint(sketch, "E14.center", {"position": v(0, 0) * mm});
            skLineSegment(sketch, "E15.1.0", {"start": v(0.97, 8.67) * mm, "end": v(7.03, 5.18) * mm});
            skLineSegment(sketch, "E15.1.1", {"start": v(1.97, 10.4) * mm, "end": v(8.03, 6.91) * mm});
            skLineSegment(sketch, "E15.1.2", {"start": v(3.47, 13) * mm, "end": v(9.53, 9.5) * mm});
            skLineSegment(sketch, "E15.1.3", {"start": v(4.47, 14.74) * mm, "end": v(10.53, 11.24) * mm});
            skLineSegment(sketch, "E15.1.4", {"start": v(8.03, 6.91) * mm, "end": v(10.53, 11.24) * mm, "construction": true});
            skLineSegment(sketch, "E15.1.5", {"start": v(5.97, 17.34) * mm, "end": v(12.03, 13.84) * mm});
            skLineSegment(sketch, "E15.1.6", {"start": v(6.97, 19.07) * mm, "end": v(13.03, 15.57) * mm});
            skLineSegment(sketch, "E15.1.7", {"start": v(8.47, 21.67) * mm, "end": v(14.53, 18.17) * mm});
            skLineSegment(sketch, "E15.1.8", {"start": v(9.47, 23.4) * mm, "end": v(15.53, 19.9) * mm});
            skLineSegment(sketch, "E15.1.9", {"start": v(10.97, 26) * mm, "end": v(17.03, 22.5) * mm});
            skLineSegment(sketch, "E15.1.10", {"start": v(11.97, 27.73) * mm, "end": v(18.03, 24.23) * mm});
            skLineSegment(sketch, "E15.1.11", {"start": v(7.03, 5.18) * mm, "end": v(8.03, 6.91) * mm});
            skLineSegment(sketch, "E15.1.12", {"start": v(9.53, 9.5) * mm, "end": v(10.53, 11.24) * mm});
            skLineSegment(sketch, "E15.1.13", {"start": v(12.03, 13.84) * mm, "end": v(13.03, 15.57) * mm});
            skLineSegment(sketch, "E15.1.14", {"start": v(14.53, 18.17) * mm, "end": v(15.53, 19.9) * mm});
            skLineSegment(sketch, "E15.1.15", {"start": v(17.03, 22.5) * mm, "end": v(18.03, 24.23) * mm});
            skLineSegment(sketch, "E15.1.16", {"start": v(0.97, 8.67) * mm, "end": v(1.97, 10.4) * mm});
            skLineSegment(sketch, "E15.1.17", {"start": v(3.47, 13) * mm, "end": v(4.47, 14.74) * mm});
            skLineSegment(sketch, "E15.1.18", {"start": v(5.97, 17.34) * mm, "end": v(6.97, 19.07) * mm});
            skLineSegment(sketch, "E15.1.19", {"start": v(8.47, 21.67) * mm, "end": v(9.47, 23.4) * mm});
            skLineSegment(sketch, "E15.1.20", {"start": v(10.97, 26) * mm, "end": v(11.97, 27.73) * mm});
            skLineSegment(sketch, "E15.2.0", {"start": v(-7.03, 5.18) * mm, "end": v(-0.97, 8.68) * mm});
            skLineSegment(sketch, "E15.2.1", {"start": v(-8.03, 6.91) * mm, "end": v(-1.97, 10.41) * mm});
            skLineSegment(sketch, "E15.2.2", {"start": v(-9.53, 9.51) * mm, "end": v(-3.47, 13) * mm});
            skLineSegment(sketch, "E15.2.3", {"start": v(-10.53, 11.24) * mm, "end": v(-4.47, 14.74) * mm});
            skLineSegment(sketch, "E15.2.4", {"start": v(-1.97, 10.41) * mm, "end": v(-4.47, 14.74) * mm, "construction": true});
            skLineSegment(sketch, "E15.2.5", {"start": v(-12.03, 13.84) * mm, "end": v(-5.97, 17.34) * mm});
            skLineSegment(sketch, "E15.2.6", {"start": v(-13.03, 15.57) * mm, "end": v(-6.97, 19.07) * mm});
            skLineSegment(sketch, "E15.2.7", {"start": v(-14.53, 18.17) * mm, "end": v(-8.47, 21.67) * mm});
            skLineSegment(sketch, "E15.2.8", {"start": v(-15.53, 19.9) * mm, "end": v(-9.47, 23.4) * mm});
            skLineSegment(sketch, "E15.2.9", {"start": v(-17.03, 22.5) * mm, "end": v(-10.97, 26) * mm});
            skLineSegment(sketch, "E15.2.10", {"start": v(-18.03, 24.23) * mm, "end": v(-11.97, 27.73) * mm});
            skLineSegment(sketch, "E15.2.11", {"start": v(-0.97, 8.68) * mm, "end": v(-1.97, 10.41) * mm});
            skLineSegment(sketch, "E15.2.12", {"start": v(-3.47, 13) * mm, "end": v(-4.47, 14.74) * mm});
            skLineSegment(sketch, "E15.2.13", {"start": v(-5.97, 17.34) * mm, "end": v(-6.97, 19.07) * mm});
            skLineSegment(sketch, "E15.2.14", {"start": v(-8.47, 21.67) * mm, "end": v(-9.47, 23.4) * mm});
            skLineSegment(sketch, "E15.2.15", {"start": v(-10.97, 26) * mm, "end": v(-11.97, 27.73) * mm});
            skLineSegment(sketch, "E15.2.16", {"start": v(-7.03, 5.18) * mm, "end": v(-8.03, 6.91) * mm});
            skLineSegment(sketch, "E15.2.17", {"start": v(-9.53, 9.51) * mm, "end": v(-10.53, 11.24) * mm});
            skLineSegment(sketch, "E15.2.18", {"start": v(-12.03, 13.84) * mm, "end": v(-13.03, 15.57) * mm});
            skLineSegment(sketch, "E15.2.19", {"start": v(-14.53, 18.17) * mm, "end": v(-15.53, 19.9) * mm});
            skLineSegment(sketch, "E15.2.20", {"start": v(-17.03, 22.5) * mm, "end": v(-18.03, 24.23) * mm});
            skLineSegment(sketch, "E15.3.0", {"start": v(-8, -3.5) * mm, "end": v(-8, 3.5) * mm});
            skLineSegment(sketch, "E15.3.1", {"start": v(-10, -3.5) * mm, "end": v(-10, 3.5) * mm});
            skLineSegment(sketch, "E15.3.2", {"start": v(-13, -3.5) * mm, "end": v(-13, 3.5) * mm});
            skLineSegment(sketch, "E15.3.3", {"start": v(-15, -3.5) * mm, "end": v(-15, 3.5) * mm});
            skLineSegment(sketch, "E15.3.4", {"start": v(-10, 3.5) * mm, "end": v(-15, 3.5) * mm, "construction": true});
            skLineSegment(sketch, "E15.3.5", {"start": v(-18, -3.5) * mm, "end": v(-18, 3.5) * mm});
            skLineSegment(sketch, "E15.3.6", {"start": v(-20, -3.5) * mm, "end": v(-20, 3.5) * mm});
            skLineSegment(sketch, "E15.3.7", {"start": v(-23, -3.5) * mm, "end": v(-23, 3.5) * mm});
            skLineSegment(sketch, "E15.3.8", {"start": v(-25, -3.5) * mm, "end": v(-25, 3.5) * mm});
            skLineSegment(sketch, "E15.3.9", {"start": v(-28, -3.5) * mm, "end": v(-28, 3.5) * mm});
            skLineSegment(sketch, "E15.3.10", {"start": v(-30, -3.5) * mm, "end": v(-30, 3.5) * mm});
            skLineSegment(sketch, "E15.3.11", {"start": v(-8, 3.5) * mm, "end": v(-10, 3.5) * mm});
            skLineSegment(sketch, "E15.3.12", {"start": v(-13, 3.5) * mm, "end": v(-15, 3.5) * mm});
            skLineSegment(sketch, "E15.3.13", {"start": v(-18, 3.5) * mm, "end": v(-20, 3.5) * mm});
            skLineSegment(sketch, "E15.3.14", {"start": v(-23, 3.5) * mm, "end": v(-25, 3.5) * mm});
            skLineSegment(sketch, "E15.3.15", {"start": v(-28, 3.5) * mm, "end": v(-30, 3.5) * mm});
            skLineSegment(sketch, "E15.3.16", {"start": v(-8, -3.5) * mm, "end": v(-10, -3.5) * mm});
            skLineSegment(sketch, "E15.3.17", {"start": v(-13, -3.5) * mm, "end": v(-15, -3.5) * mm});
            skLineSegment(sketch, "E15.3.18", {"start": v(-18, -3.5) * mm, "end": v(-20, -3.5) * mm});
            skLineSegment(sketch, "E15.3.19", {"start": v(-23, -3.5) * mm, "end": v(-25, -3.5) * mm});
            skLineSegment(sketch, "E15.3.20", {"start": v(-28, -3.5) * mm, "end": v(-30, -3.5) * mm});
            skLineSegment(sketch, "E15.4.0", {"start": v(-0.97, -8.67) * mm, "end": v(-7.03, -5.18) * mm});
            skLineSegment(sketch, "E15.4.1", {"start": v(-1.97, -10.4) * mm, "end": v(-8.03, -6.91) * mm});
            skLineSegment(sketch, "E15.4.2", {"start": v(-3.47, -13) * mm, "end": v(-9.53, -9.5) * mm});
            skLineSegment(sketch, "E15.4.3", {"start": v(-4.47, -14.74) * mm, "end": v(-10.53, -11.24) * mm});
            skLineSegment(sketch, "E15.4.4", {"start": v(-8.03, -6.91) * mm, "end": v(-10.53, -11.24) * mm, "construction": true});
            skLineSegment(sketch, "E15.4.5", {"start": v(-5.97, -17.34) * mm, "end": v(-12.03, -13.84) * mm});
            skLineSegment(sketch, "E15.4.6", {"start": v(-6.97, -19.07) * mm, "end": v(-13.03, -15.57) * mm});
            skLineSegment(sketch, "E15.4.7", {"start": v(-8.47, -21.67) * mm, "end": v(-14.53, -18.17) * mm});
            skLineSegment(sketch, "E15.4.8", {"start": v(-9.47, -23.4) * mm, "end": v(-15.53, -19.9) * mm});
            skLineSegment(sketch, "E15.4.9", {"start": v(-10.97, -26) * mm, "end": v(-17.03, -22.5) * mm});
            skLineSegment(sketch, "E15.4.10", {"start": v(-11.97, -27.73) * mm, "end": v(-18.03, -24.23) * mm});
            skLineSegment(sketch, "E15.4.11", {"start": v(-7.03, -5.18) * mm, "end": v(-8.03, -6.91) * mm});
            skLineSegment(sketch, "E15.4.12", {"start": v(-9.53, -9.5) * mm, "end": v(-10.53, -11.24) * mm});
            skLineSegment(sketch, "E15.4.13", {"start": v(-12.03, -13.84) * mm, "end": v(-13.03, -15.57) * mm});
            skLineSegment(sketch, "E15.4.14", {"start": v(-14.53, -18.17) * mm, "end": v(-15.53, -19.9) * mm});
            skLineSegment(sketch, "E15.4.15", {"start": v(-17.03, -22.5) * mm, "end": v(-18.03, -24.23) * mm});
            skLineSegment(sketch, "E15.4.16", {"start": v(-0.97, -8.67) * mm, "end": v(-1.97, -10.4) * mm});
            skLineSegment(sketch, "E15.4.17", {"start": v(-3.47, -13) * mm, "end": v(-4.47, -14.74) * mm});
            skLineSegment(sketch, "E15.4.18", {"start": v(-5.97, -17.34) * mm, "end": v(-6.97, -19.07) * mm});
            skLineSegment(sketch, "E15.4.19", {"start": v(-8.47, -21.67) * mm, "end": v(-9.47, -23.4) * mm});
            skLineSegment(sketch, "E15.4.20", {"start": v(-10.97, -26) * mm, "end": v(-11.97, -27.73) * mm});
            skLineSegment(sketch, "E15.5.0", {"start": v(7.03, -5.18) * mm, "end": v(0.97, -8.68) * mm});
            skLineSegment(sketch, "E15.5.1", {"start": v(8.03, -6.91) * mm, "end": v(1.97, -10.41) * mm});
            skLineSegment(sketch, "E15.5.2", {"start": v(9.53, -9.51) * mm, "end": v(3.47, -13) * mm});
            skLineSegment(sketch, "E15.5.3", {"start": v(10.53, -11.24) * mm, "end": v(4.47, -14.74) * mm});
            skLineSegment(sketch, "E15.5.4", {"start": v(1.97, -10.41) * mm, "end": v(4.47, -14.74) * mm, "construction": true});
            skLineSegment(sketch, "E15.5.5", {"start": v(12.03, -13.84) * mm, "end": v(5.97, -17.34) * mm});
            skLineSegment(sketch, "E15.5.6", {"start": v(13.03, -15.57) * mm, "end": v(6.97, -19.07) * mm});
            skLineSegment(sketch, "E15.5.7", {"start": v(14.53, -18.17) * mm, "end": v(8.47, -21.67) * mm});
            skLineSegment(sketch, "E15.5.8", {"start": v(15.53, -19.9) * mm, "end": v(9.47, -23.4) * mm});
            skLineSegment(sketch, "E15.5.9", {"start": v(17.03, -22.5) * mm, "end": v(10.97, -26) * mm});
            skLineSegment(sketch, "E15.5.10", {"start": v(18.03, -24.23) * mm, "end": v(11.97, -27.73) * mm});
            skLineSegment(sketch, "E15.5.11", {"start": v(0.97, -8.68) * mm, "end": v(1.97, -10.41) * mm});
            skLineSegment(sketch, "E15.5.12", {"start": v(3.47, -13) * mm, "end": v(4.47, -14.74) * mm});
            skLineSegment(sketch, "E15.5.13", {"start": v(5.97, -17.34) * mm, "end": v(6.97, -19.07) * mm});
            skLineSegment(sketch, "E15.5.14", {"start": v(8.47, -21.67) * mm, "end": v(9.47, -23.4) * mm});
            skLineSegment(sketch, "E15.5.15", {"start": v(10.97, -26) * mm, "end": v(11.97, -27.73) * mm});
            skLineSegment(sketch, "E15.5.16", {"start": v(7.03, -5.18) * mm, "end": v(8.03, -6.91) * mm});
            skLineSegment(sketch, "E15.5.17", {"start": v(9.53, -9.51) * mm, "end": v(10.53, -11.24) * mm});
            skLineSegment(sketch, "E15.5.18", {"start": v(12.03, -13.84) * mm, "end": v(13.03, -15.57) * mm});
            skLineSegment(sketch, "E15.5.19", {"start": v(14.53, -18.17) * mm, "end": v(15.53, -19.9) * mm});
            skLineSegment(sketch, "E15.5.20", {"start": v(17.03, -22.5) * mm, "end": v(18.03, -24.23) * mm});
            skSolve(sketch);
        }
        {
            var Q0;
            Q0=makeQuery(id+"F4.imprint","IMPRINT",FACE,{"disambiguationData":[TD([[makeQuery(id+"F4.imprint","IMPRINT",EDGE,{"derivedFrom":sQuery(id+"F4.wireOp",EDGE,"E14.2.0")}),-1.0]])]});
            var Q1;
            Q1=makeQuery(id+"F4.imprint","IMPRINT",FACE,{"disambiguationData":[TD([[makeQuery(id+"F4.imprint","IMPRINT",EDGE,{"derivedFrom":sQuery(id+"F4.wireOp",EDGE,"E15.2.9")}),1.0]])]});
            var Q2;
            Q2=makeQuery(id+"F4.imprint","IMPRINT",FACE,{"disambiguationData":[TD([[makeQuery(id+"F4.imprint","IMPRINT",EDGE,{"derivedFrom":sQuery(id+"F4.wireOp",EDGE,"E15.2.7")}),1.0]])]});
            var Q3;
            Q3=makeQuery(id+"F4.imprint","IMPRINT",FACE,{"disambiguationData":[TD([[makeQuery(id+"F4.imprint","IMPRINT",EDGE,{"derivedFrom":sQuery(id+"F4.wireOp",EDGE,"E15.2.5")}),1.0]])]});
            var Q4;
            Q4=makeQuery(id+"F4.imprint","IMPRINT",FACE,{"disambiguationData":[TD([[makeQuery(id+"F4.imprint","IMPRINT",EDGE,{"derivedFrom":sQuery(id+"F4.wireOp",EDGE,"E15.2.2")}),1.0]])]});
            var Q5;
            Q5=makeQuery(id+"F4.imprint","IMPRINT",FACE,{"disambiguationData":[TD([[makeQuery(id+"F4.imprint","IMPRINT",EDGE,{"derivedFrom":sQuery(id+"F4.wireOp",EDGE,"E15.2.0")}),1.0]])]});
            var Q6;
            Q6=makeQuery(id+"F4.imprint","IMPRINT",FACE,{"disambiguationData":[TD([[makeQuery(id+"F4.imprint","IMPRINT",EDGE,{"derivedFrom":sQuery(id+"F4.wireOp",EDGE,"E14.1.0")}),-1.0]])]});
            var Q7;
            Q7=makeQuery(id+"F4.imprint","IMPRINT",FACE,{"disambiguationData":[TD([[makeQuery(id+"F4.imprint","IMPRINT",EDGE,{"derivedFrom":sQuery(id+"F4.wireOp",EDGE,"E15.1.9")}),1.0]])]});
            var Q8;
            Q8=makeQuery(id+"F4.imprint","IMPRINT",FACE,{"disambiguationData":[TD([[makeQuery(id+"F4.imprint","IMPRINT",EDGE,{"derivedFrom":sQuery(id+"F4.wireOp",EDGE,"E15.1.7")}),1.0]])]});
            var Q9;
            Q9=makeQuery(id+"F4.imprint","IMPRINT",FACE,{"disambiguationData":[TD([[makeQuery(id+"F4.imprint","IMPRINT",EDGE,{"derivedFrom":sQuery(id+"F4.wireOp",EDGE,"E15.1.5")}),1.0]])]});
            var Q10;
            Q10=makeQuery(id+"F4.imprint","IMPRINT",FACE,{"disambiguationData":[TD([[makeQuery(id+"F4.imprint","IMPRINT",EDGE,{"derivedFrom":sQuery(id+"F4.wireOp",EDGE,"E15.1.2")}),1.0]])]});
            var Q11;
            Q11=makeQuery(id+"F4.imprint","IMPRINT",FACE,{"disambiguationData":[TD([[makeQuery(id+"F4.imprint","IMPRINT",EDGE,{"derivedFrom":sQuery(id+"F4.wireOp",EDGE,"E15.1.0")}),1.0]])]});
            var Q12;
            Q12=makeQuery(id+"F4.imprint","IMPRINT",FACE,{"disambiguationData":[TD([[makeQuery(id+"F4.imprint","IMPRINT",EDGE,{"derivedFrom":sQuery(id+"F4.wireOp",EDGE,"E10.bottom")}),-1.0]])]});
            var Q13;
            Q13=makeQuery(id+"F4.imprint","IMPRINT",FACE,{"disambiguationData":[TD([[makeQuery(id+"F4.imprint","IMPRINT",EDGE,{"derivedFrom":sQuery(id+"F4.wireOp",EDGE,"E11.1.0.0")}),-1.0]])]});
            var Q14;
            Q14=makeQuery(id+"F4.imprint","IMPRINT",FACE,{"disambiguationData":[TD([[makeQuery(id+"F4.imprint","IMPRINT",EDGE,{"derivedFrom":sQuery(id+"F4.wireOp",EDGE,"E11.2.0.0")}),-1.0]])]});
            var Q15;
            Q15=makeQuery(id+"F4.imprint","IMPRINT",FACE,{"disambiguationData":[TD([[makeQuery(id+"F4.imprint","IMPRINT",EDGE,{"derivedFrom":sQuery(id+"F4.wireOp",EDGE,"E11.3.0.0")}),-1.0]])]});
            var Q16;
            Q16=makeQuery(id+"F4.imprint","IMPRINT",FACE,{"disambiguationData":[TD([[makeQuery(id+"F4.imprint","IMPRINT",EDGE,{"derivedFrom":sQuery(id+"F4.wireOp",EDGE,"E11.4.0.0")}),-1.0]])]});
            var Q17;
            Q17=makeQuery(id+"F4.imprint","IMPRINT",FACE,{"disambiguationData":[TD([[makeQuery(id+"F4.imprint","IMPRINT",EDGE,{"derivedFrom":sQuery(id+"F4.wireOp",EDGE,"E12")}),-1.0]])]});
            var Q18;
            Q18=makeQuery(id+"F4.imprint","IMPRINT",FACE,{"disambiguationData":[TD([[makeQuery(id+"F4.imprint","IMPRINT",EDGE,{"derivedFrom":sQuery(id+"F4.wireOp",EDGE,"E15.3.7")}),1.0]])]});
            var Q19;
            Q19=makeQuery(id+"F4.imprint","IMPRINT",FACE,{"disambiguationData":[TD([[makeQuery(id+"F4.imprint","IMPRINT",EDGE,{"derivedFrom":sQuery(id+"F4.wireOp",EDGE,"E15.3.5")}),1.0]])]});
            var Q20;
            Q20=makeQuery(id+"F4.imprint","IMPRINT",FACE,{"disambiguationData":[TD([[makeQuery(id+"F4.imprint","IMPRINT",EDGE,{"derivedFrom":sQuery(id+"F4.wireOp",EDGE,"E15.3.2")}),1.0]])]});
            var Q21;
            Q21=makeQuery(id+"F4.imprint","IMPRINT",FACE,{"disambiguationData":[TD([[makeQuery(id+"F4.imprint","IMPRINT",EDGE,{"derivedFrom":sQuery(id+"F4.wireOp",EDGE,"E15.3.0")}),1.0]])]});
            var Q22;
            Q22=makeQuery(id+"F4.imprint","IMPRINT",FACE,{"disambiguationData":[TD([[makeQuery(id+"F4.imprint","IMPRINT",EDGE,{"derivedFrom":sQuery(id+"F4.wireOp",EDGE,"E14.3.0")}),-1.0]])]});
            var Q23;
            Q23=makeQuery(id+"F4.imprint","IMPRINT",FACE,{"disambiguationData":[TD([[makeQuery(id+"F4.imprint","IMPRINT",EDGE,{"derivedFrom":sQuery(id+"F4.wireOp",EDGE,"E15.3.9")}),1.0]])]});
            var Q24;
            Q24=makeQuery(id+"F4.imprint","IMPRINT",FACE,{"disambiguationData":[TD([[makeQuery(id+"F4.imprint","IMPRINT",EDGE,{"derivedFrom":sQuery(id+"F4.wireOp",EDGE,"E14.4.0")}),-1.0]])]});
            var Q25;
            Q25=makeQuery(id+"F4.imprint","IMPRINT",FACE,{"disambiguationData":[TD([[makeQuery(id+"F4.imprint","IMPRINT",EDGE,{"derivedFrom":sQuery(id+"F4.wireOp",EDGE,"E15.4.9")}),1.0]])]});
            var Q26;
            Q26=makeQuery(id+"F4.imprint","IMPRINT",FACE,{"disambiguationData":[TD([[makeQuery(id+"F4.imprint","IMPRINT",EDGE,{"derivedFrom":sQuery(id+"F4.wireOp",EDGE,"E15.4.7")}),1.0]])]});
            var Q27;
            Q27=makeQuery(id+"F4.imprint","IMPRINT",FACE,{"disambiguationData":[TD([[makeQuery(id+"F4.imprint","IMPRINT",EDGE,{"derivedFrom":sQuery(id+"F4.wireOp",EDGE,"E15.4.5")}),1.0]])]});
            var Q28;
            Q28=makeQuery(id+"F4.imprint","IMPRINT",FACE,{"disambiguationData":[TD([[makeQuery(id+"F4.imprint","IMPRINT",EDGE,{"derivedFrom":sQuery(id+"F4.wireOp",EDGE,"E15.4.2")}),1.0]])]});
            var Q29;
            Q29=makeQuery(id+"F4.imprint","IMPRINT",FACE,{"disambiguationData":[TD([[makeQuery(id+"F4.imprint","IMPRINT",EDGE,{"derivedFrom":sQuery(id+"F4.wireOp",EDGE,"E15.4.0")}),1.0]])]});
            var Q30;
            Q30=makeQuery(id+"F4.imprint","IMPRINT",FACE,{"disambiguationData":[TD([[makeQuery(id+"F4.imprint","IMPRINT",EDGE,{"derivedFrom":sQuery(id+"F4.wireOp",EDGE,"E15.5.0")}),1.0]])]});
            var Q31;
            Q31=makeQuery(id+"F4.imprint","IMPRINT",FACE,{"disambiguationData":[TD([[makeQuery(id+"F4.imprint","IMPRINT",EDGE,{"derivedFrom":sQuery(id+"F4.wireOp",EDGE,"E15.5.2")}),1.0]])]});
            var Q32;
            Q32=makeQuery(id+"F4.imprint","IMPRINT",FACE,{"disambiguationData":[TD([[makeQuery(id+"F4.imprint","IMPRINT",EDGE,{"derivedFrom":sQuery(id+"F4.wireOp",EDGE,"E15.5.5")}),1.0]])]});
            var Q33;
            Q33=makeQuery(id+"F4.imprint","IMPRINT",FACE,{"disambiguationData":[TD([[makeQuery(id+"F4.imprint","IMPRINT",EDGE,{"derivedFrom":sQuery(id+"F4.wireOp",EDGE,"E15.5.9")}),1.0]])]});
            var Q34;
            Q34=makeQuery(id+"F4.imprint","IMPRINT",FACE,{"disambiguationData":[TD([[makeQuery(id+"F4.imprint","IMPRINT",EDGE,{"derivedFrom":sQuery(id+"F4.wireOp",EDGE,"E14.5.0")}),-1.0]])]});
            var Q35;
            Q35=makeQuery(id+"F4.imprint","IMPRINT",FACE,{"disambiguationData":[TD([[makeQuery(id+"F4.imprint","IMPRINT",EDGE,{"derivedFrom":sQuery(id+"F4.wireOp",EDGE,"E15.5.7")}),1.0]])]});
            extrude(context, id + "F5", {"entities" : qUnion([Q0, Q1, Q2, Q3, Q4, Q5, Q6, Q7, Q8, Q9, Q10, Q11, Q12, Q13, Q14, Q15, Q16, Q17, Q18, Q19, Q20, Q21, Q22, Q23, Q24, Q25, Q26, Q27, Q28, Q29, Q30, Q31, Q32, Q33, Q34, Q35]), "operationType" : NewBodyOperationType.REMOVE, "oppositeDirection" : true, "depth" : 1 * mm, "offsetDistance" : 25 * mm});
        }
    });
